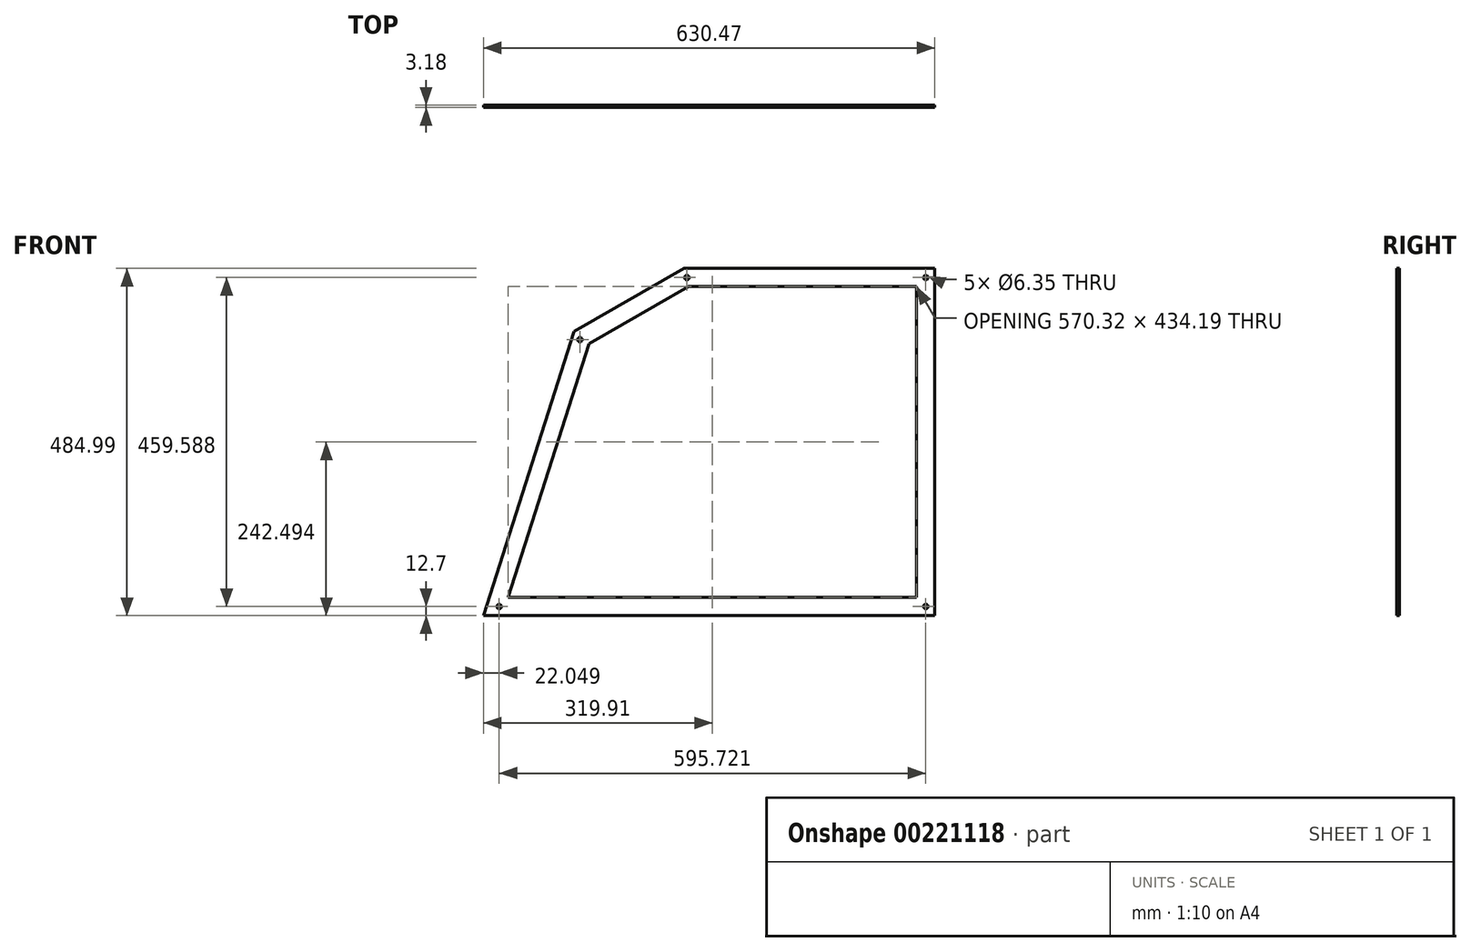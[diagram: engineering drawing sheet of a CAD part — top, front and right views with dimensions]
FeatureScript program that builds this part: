
annotation { "Feature Type Name" : "Feature", "Feature Type Description" : "" }
export const myFeature = defineFeature(function(context is Context, id is Id, definition is map)
    precondition{}
    {
        {
            var Q0;
            Q0=qCreatedBy(makeId("Front.planeOp"),FACE);
            var sketch = newSketch(context, id + "F0", { "sketchPlane" : qUnion([Q0])});
            skLineSegment(sketch, "E0", {"start": v(-630.47, 0) * mm, "end": v(0, 0) * mm});
            skLineSegment(sketch, "E1", {"start": v(0, 0) * mm, "end": v(0, 484.99) * mm});
            skLineSegment(sketch, "E2", {"start": v(0, 484.99) * mm, "end": v(-350.4, 484.99) * mm});
            skLineSegment(sketch, "E3", {"start": v(-350.4, 484.99) * mm, "end": v(-504.1, 396.78) * mm});
            skLineSegment(sketch, "E4", {"start": v(-504.1, 396.78) * mm, "end": v(-630.47, 0) * mm});
            skLineSegment(sketch, "E5.0", {"start": v(-482.9, 379.66) * mm, "end": v(-595.72, 25.4) * mm});
            skLineSegment(sketch, "E5.1", {"start": v(-343.63, 459.59) * mm, "end": v(-482.9, 379.66) * mm});
            skLineSegment(sketch, "E5.2", {"start": v(-595.72, 25.4) * mm, "end": v(-25.4, 25.4) * mm});
            skLineSegment(sketch, "E5.3", {"start": v(-25.4, 25.4) * mm, "end": v(-25.4, 459.59) * mm});
            skLineSegment(sketch, "E5.4", {"start": v(-25.4, 459.59) * mm, "end": v(-343.63, 459.59) * mm});
            skSolve(sketch);
        }
        {
            var Q0;
            Q0 = qSketchRegion(id + "F0", true);
            extrude(context, id + "F1", {"entities" : qUnion([Q0]), "depth" : 1.59 * mm, "hasSecondDirection" : true, "secondDirectionOppositeDirection" : true, "secondDirectionDepth" : 1.59 * mm});
        }
        {
            var Q0;
            Q0=makeQuery(id+"F1.opExtrude","CAP_FACE",FACE,{"disambiguationData":[OSD([sQuery(id+"F0.wireOp",EDGE,"E0"),sQuery(id+"F0.wireOp",EDGE,"E1"),sQuery(id+"F0.wireOp",EDGE,"E2"),sQuery(id+"F0.wireOp",EDGE,"E3"),sQuery(id+"F0.wireOp",EDGE,"E4"),sQuery(id+"F0.wireOp",EDGE,"E5.0"),sQuery(id+"F0.wireOp",EDGE,"E5.1"),sQuery(id+"F0.wireOp",EDGE,"E5.2"),sQuery(id+"F0.wireOp",EDGE,"E5.3"),sQuery(id+"F0.wireOp",EDGE,"E5.4")])],"isStart":false});
            var sketch = newSketch(context, id + "F2", { "sketchPlane" : qUnion([Q0])});
            skCircle(sketch, "E6", {"center": v(-12.7, 12.7) * mm, "radius": 3.17 * mm});
            skCircle(sketch, "E7", {"center": v(-12.7, 472.29) * mm, "radius": 3.18 * mm});
            skCircle(sketch, "E8", {"center": v(-346.21, 472.29) * mm, "radius": 3.17 * mm});
            skCircle(sketch, "E9", {"center": v(-495.6, 385.6) * mm, "radius": 3.18 * mm});
            skCircle(sketch, "E10", {"center": v(-608.42, 12.7) * mm, "radius": 3.18 * mm});
            skSolve(sketch);
        }
        {
            var Q0;
            Q0 = qSketchRegion(id + "F2", true);
            var Q1;
            Q1=makeQuery(id+"F1.opExtrude","CAP_FACE",FACE,{"disambiguationData":[OSD([sQuery(id+"F0.wireOp",EDGE,"E0"),sQuery(id+"F0.wireOp",EDGE,"E1"),sQuery(id+"F0.wireOp",EDGE,"E2"),sQuery(id+"F0.wireOp",EDGE,"E3"),sQuery(id+"F0.wireOp",EDGE,"E4"),sQuery(id+"F0.wireOp",EDGE,"E5.0"),sQuery(id+"F0.wireOp",EDGE,"E5.1"),sQuery(id+"F0.wireOp",EDGE,"E5.2"),sQuery(id+"F0.wireOp",EDGE,"E5.3"),sQuery(id+"F0.wireOp",EDGE,"E5.4")])],"isStart":true});
            extrude(context, id + "F3", {"entities" : qUnion([Q0]), "operationType" : NewBodyOperationType.REMOVE, "endBound" : BoundingType.UP_TO_SURFACE, "oppositeDirection" : true, "endBoundEntityFace" : qUnion([Q1]), "depth" : 25.4 * mm});
        }
    });
